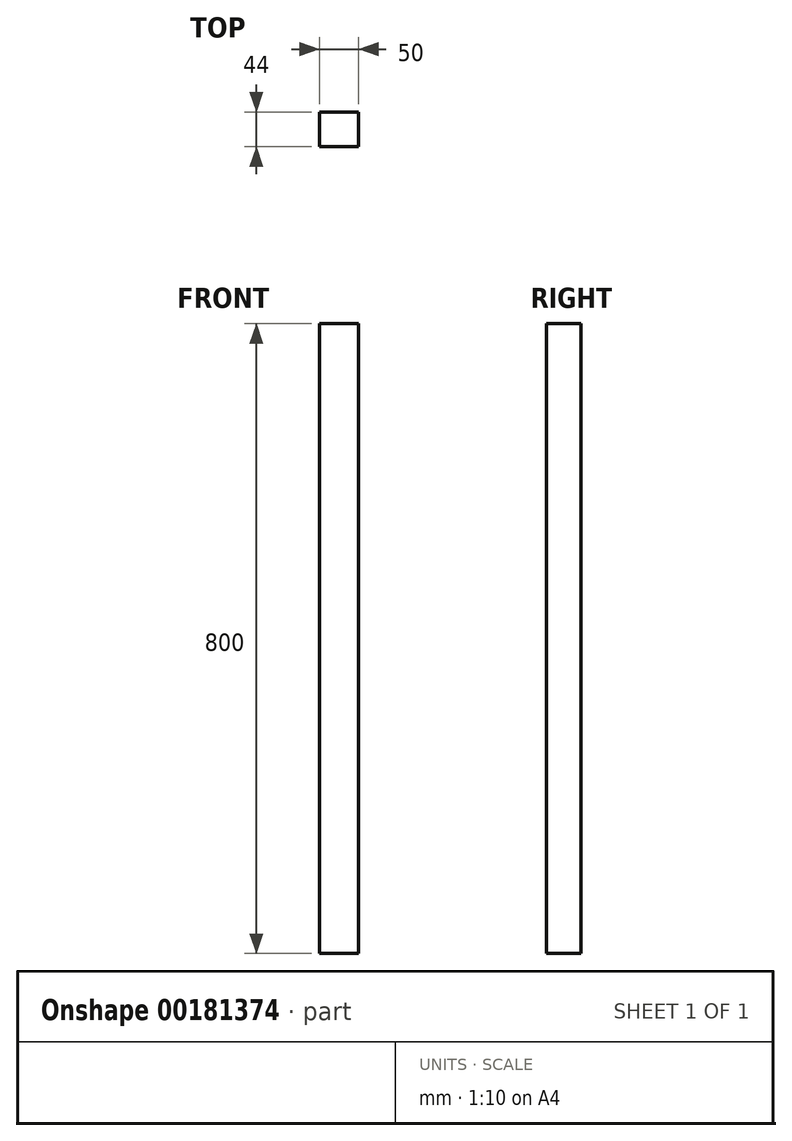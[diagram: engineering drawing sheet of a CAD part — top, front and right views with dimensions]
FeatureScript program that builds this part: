
annotation { "Feature Type Name" : "Feature", "Feature Type Description" : "" }
export const myFeature = defineFeature(function(context is Context, id is Id, definition is map)
    precondition{}
    {
        {
            var Q0;
            Q0=qCreatedBy(makeId("Top.planeOp"),FACE);
            var sketch = newSketch(context, id + "F0", { "sketchPlane" : qUnion([Q0])});
            skLineSegment(sketch, "E0.bottom", {"start": v(-25, 22) * mm, "end": v(25, 22) * mm});
            skLineSegment(sketch, "E0.top", {"start": v(-25, -22) * mm, "end": v(25, -22) * mm});
            skLineSegment(sketch, "E0.left", {"start": v(-25, 22) * mm, "end": v(-25, -22) * mm});
            skLineSegment(sketch, "E0.right", {"start": v(25, 22) * mm, "end": v(25, -22) * mm});
            skPoint(sketch, "E0.middle", {"position": v(0, 0) * mm});
            skSolve(sketch);
        }
        {
            var Q0;
            Q0 = qSketchRegion(id + "F0", true);
            extrude(context, id + "F1", {"entities" : qUnion([Q0]), "endBound" : BoundingType.SYMMETRIC, "depth" : 800 * mm});
        }
    });
